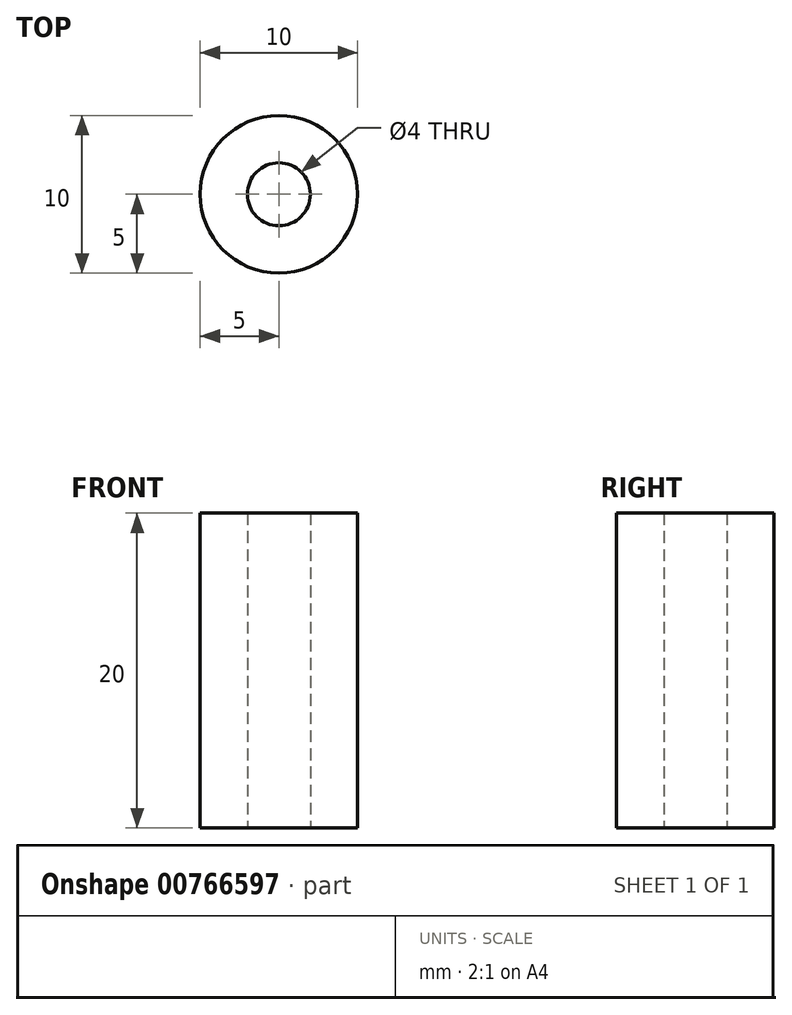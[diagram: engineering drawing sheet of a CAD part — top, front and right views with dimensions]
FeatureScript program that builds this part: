
annotation { "Feature Type Name" : "Feature", "Feature Type Description" : "" }
export const myFeature = defineFeature(function(context is Context, id is Id, definition is map)
    precondition{}
    {
        {
            var Q0;
            Q0=qCreatedBy(makeId("Top.planeOp"),FACE);
            var sketch = newSketch(context, id + "F0", { "sketchPlane" : qUnion([Q0])});
            skCircle(sketch, "E0", {"center": v(0, 0) * mm, "radius": 2 * mm});
            skCircle(sketch, "E1", {"center": v(0, 0) * mm, "radius": 5 * mm});
            skSolve(sketch);
        }
        {
            var Q0;
            Q0 = qSketchRegion(id + "F0", true);
            extrude(context, id + "F1", {"entities" : qUnion([Q0]), "depth" : 20 * mm, "offsetDistance" : 25 * mm});
        }
    });
